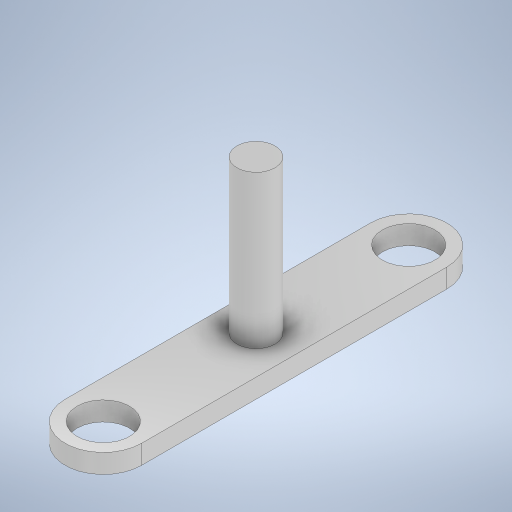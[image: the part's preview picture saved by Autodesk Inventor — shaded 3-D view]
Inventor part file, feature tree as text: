
AUTODESK INVENTOR PART (.ipt)
format: ipt  version: 2024 (Build 280153000, 153)  size: 262,144 bytes
history: native  units: in
note: dims shown in document units (in); Inventor stores cm internally (conversion verified against a paired STEP export)
features: extrude x2, sketch x2
ambient origin geometry x8: Origin, YZ Plane, XZ Plane, XY Plane, X Axis, Y Axis, Z Axis, Center Point
bodies: Body1 (feature_tree)
feature tree (4):
  extrude  "Extrusion13"  Depth=1.0in
  extrude  "Extrusion14"  Depth=2.0in
  sketch  "Sketch10"  dims[d70=0.688in d71=1.0in]
  sketch  "Sketch11"  dims[d72=4.0in d74=0.688in d75=1.0in d76=4.0in d78=0.5in d79=0.25in d80=0.0in d81=0.5in d82=2.0in d83=0.5in d84=2.0in d85=0.0in]
